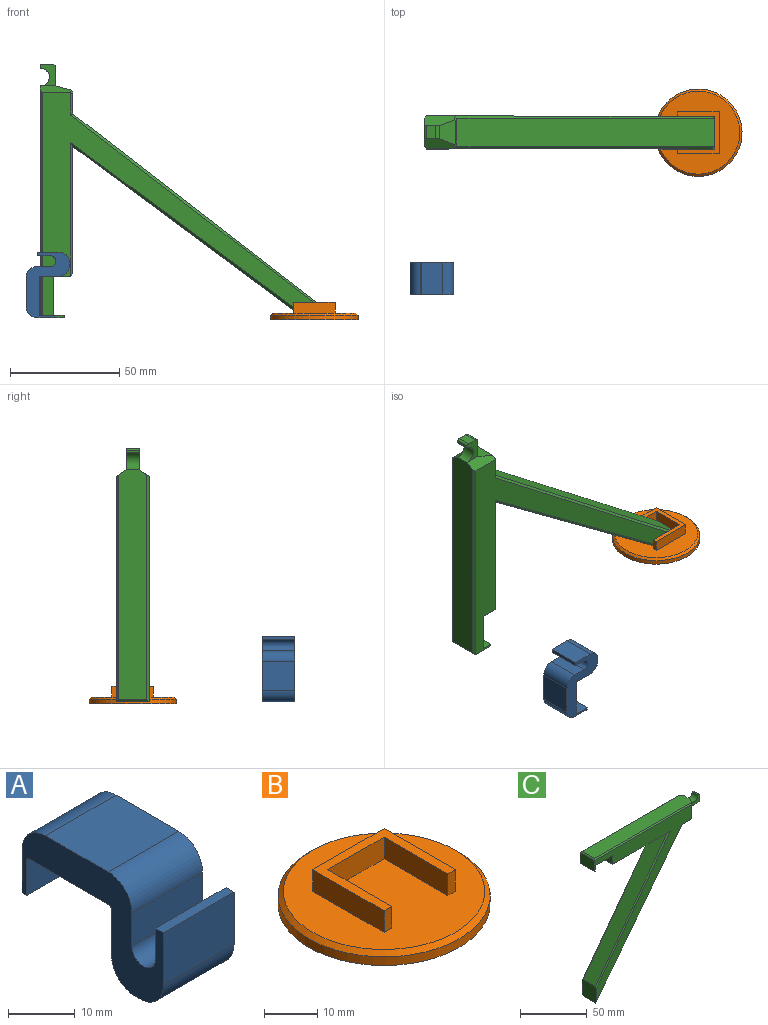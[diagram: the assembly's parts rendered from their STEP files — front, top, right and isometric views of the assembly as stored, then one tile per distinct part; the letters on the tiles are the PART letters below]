
ASSEMBLY  parts=3 mates=2
PART A: 20 faces, bbox 15x30x20 mm
  f0: plane 30x20mm, normal (1,0,0), area 245.4mm2, adj f2,f3,f4,f5,f6,f7,f8,f9
  f1: plane 30x20mm, normal (-1,0,0), area 245.4mm2, adj f2,f3,f4,f5,f6,f7,f8,f9
  f2: plane 15x1mm, normal (0,0,-1), area 15mm2, adj f0,f1,f15,f17
  f3: plane 15x8mm, normal (0,1,0), area 120mm2, adj f0,f1,f9,f16
  f4: plane 15x13.32mm, normal (0,0,1), area 199.8mm2, adj f0,f1,f14,f16
  f5: plane 15x9.64mm, normal (0,-1,0), area 144.7mm2, adj f0,f1,f13,f17
  f6: plane 15x5.74mm, normal (0,1,0), area 86mm2, adj f0,f1,f7,f13
  f7: cylinder r=2.5mm len=15mm, axis (1,0,0), area 117.8mm2, adj f0,f1,f6,f8
  f8: plane 15x6.09mm, normal (0,-1,0), area 91.4mm2, adj f0,f1,f7,f14
  f9: plane 15x1mm, normal (0,0,-1), area 15mm2, adj f0,f1,f3,f10
  f10: plane 15x6.5mm, normal (0,-1,0), area 97.5mm2, adj f0,f1,f9,f18
  f11: plane 17x15mm, normal (0,0,-1), area 255mm2, adj f0,f1,f18,f19
  f12: plane 15x8.5mm, normal (0,1,0), area 127.5mm2, adj f0,f1,f15,f19
  f13: plane 15x1.68mm, normal (0,0,1), area 25.2mm2, adj f0,f1,f5,f6
  f14: cylinder r=5mm len=15mm, axis (-1,0,0), area 117.8mm2, adj f0,f1,f4,f8
  f15: cylinder r=5mm len=15mm, axis (-1,0,0), area 117.8mm2, adj f0,f1,f2,f12
  f16: cylinder r=5mm len=15mm, axis (-1,0,0), area 117.8mm2, adj f0,f1,f3,f4
  f17: cylinder r=5mm len=15mm, axis (-1,0,0), area 117.8mm2, adj f0,f1,f2,f5
  f18: cylinder r=0.5mm len=15mm, axis (-1,0,0), area 11.8mm2, adj f0,f1,f10,f11
  f19: cylinder r=0.5mm len=15mm, axis (1,0,0), area 11.8mm2, adj f0,f1,f11,f12
PART B: 13 faces, bbox 40x40x8 mm
  f0: plane 5x2mm, normal (0,-1,0), area 10mm2, adj f1,f6,f10,f12
  f1: plane 19x19mm, normal (0,0,1), area 106mm2, adj f0,f5,f6,f7,f8,f9,f10,f11
  f2: cylinder r=20mm len=40mm, axis (0,0,1), area 251.3mm2, adj f3,f4
  f3: plane 40x40mm, normal (0,0,-1), area 1256.6mm2, adj f2
  f4: cone r=19mm half-angle=45deg, axis (0,0,-1), area 173.3mm2, adj f2,f12
  f5: plane 15x5mm, normal (0,-1,0), area 75mm2, adj f1,f6,f11,f12
  f6: plane 17x5mm, normal (-1,0,0), area 85mm2, adj f0,f1,f5,f12
  f7: plane 19x5mm, normal (0,1,0), area 95mm2, adj f1,f8,f10,f12
  f8: plane 19x5mm, normal (-1,0,0), area 95mm2, adj f1,f7,f9,f12
  f9: plane 5x2mm, normal (0,-1,0), area 10mm2, adj f1,f8,f11,f12
  f10: plane 19x5mm, normal (1,0,0), area 95mm2, adj f0,f1,f7,f12
  f11: plane 17x5mm, normal (1,0,0), area 85mm2, adj f1,f5,f9,f12
  f12: plane 38x38mm, normal (0,0,1), area 1028.1mm2, adj f0,f4,f5,f6,f7,f8,f9,f10
PART C: 39 faces, bbox 116x15x133 mm
  f0: plane 6x0.94mm, normal (0,0,1), area 5.6mm2, adj f6,f7,f26,f28
  f1: plane 105.07x13mm, normal (0,0,1), area 1357.6mm2, adj f7,f25,f27,f29,f35,f36
  f2: plane 11.33x7.25mm, normal (0.97,0,-0.25), area 65.5mm2, adj f3,f27,f29,f32,f33,f34
  f3: plane 9.05x6mm, normal (0,0,-1), area 54.3mm2, adj f2,f4,f26,f28
  f4: cylinder r=2mm len=6mm, axis (0,-1,0), area 11.7mm2, adj f3,f5,f26,f28
  f5: plane 6x4.35mm, normal (1,0,0), area 26.1mm2, adj f4,f6,f26,f28
  f6: cylinder r=1mm len=6mm, axis (0,-1,0), area 9.4mm2, adj f0,f5,f26,f28
  f7: cylinder r=4mm len=8mm, axis (0,-1,0), area 77.8mm2, adj f0,f1,f26,f27,f28,f29
  f8: plane 130.37x103.01mm, normal (0,-1,0), area 2384mm2, adj f11,f12,f13,f14,f16,f18,f22,f23
  f9: plane 13x10.02mm, normal (0,0,-1), area 129.4mm2, adj f19,f30,f31,f32,f33,f34
  f10: plane 130.37x103.01mm, normal (0,1,0), area 2384mm2, adj f11,f12,f13,f14,f16,f18,f20,f21
  f11: plane 15x5mm, normal (1,0,0), area 75mm2, adj f8,f10,f12,f14
  f12: plane 18x15mm, normal (0,0,-1), area 270mm2, adj f8,f10,f11,f16
  f13: plane 15x10mm, normal (-1,0,0), area 150mm2, adj f8,f10,f14,f25
  f14: plane 15x1mm, normal (0,0,-1), area 15mm2, adj f8,f10,f11,f13
  f15: plane 58.21x13mm, normal (0,0,-1), area 756.7mm2, adj f17,f24,f37,f38
  f16: plane 15x8mm, normal (-1,0,0), area 120mm2, adj f8,f10,f12,f24
  f17: plane 103x76.21mm, normal (-0.8,0,0.59), area 1665.6mm2, adj f15,f18,f21,f23
  f18: plane 15x15mm, normal (-1,0,0), area 221.7mm2, adj f8,f10,f17,f19,f20,f21,f22,f23
  f19: plane 118x91.21mm, normal (0.79,0,-0.61), area 1938.8mm2, adj f9,f18,f20,f22
  f20: plane 119x91.21mm, normal (0.56,0.71,-0.43), area 210.3mm2, adj f10,f18,f19,f30
  f21: plane 105.68x78.19mm, normal (-0.57,0.71,0.42), area 183.6mm2, adj f10,f17,f18,f37
  f22: plane 119x91.21mm, normal (0.56,-0.71,-0.43), area 210.3mm2, adj f8,f18,f19,f31
  f23: plane 105.68x78.19mm, normal (-0.57,-0.71,0.42), area 183.6mm2, adj f8,f17,f18,f38
  f24: plane 15x1mm, normal (-0.71,0,-0.71), area 19.8mm2, adj f15,f16,f37,f38
  f25: plane 15x1mm, normal (-0.71,0,0.71), area 19.8mm2, adj f1,f13,f35,f36
  f26: plane 9.93x7mm, normal (0,-1,0), area 42.1mm2, adj f0,f3,f4,f5,f6,f7,f27
  f27: plane 14.02x4.52mm, normal (0.83,-0.56,0), area 64.3mm2, adj f1,f2,f7,f8,f26,f33,f35
  f28: plane 9.93x7mm, normal (0,1,0), area 42.1mm2, adj f0,f3,f4,f5,f6,f7,f29
  f29: plane 14.02x4.52mm, normal (0.83,0.56,0), area 64.3mm2, adj f1,f2,f7,f10,f28,f32,f36
  f30: plane 10.3x1mm, normal (0,0.71,-0.71), area 13.8mm2, adj f9,f10,f20,f32
  f31: plane 10.3x1mm, normal (0,-0.71,-0.71), area 13.8mm2, adj f8,f9,f22,f33
  f32: plane 2.18x1.77mm, normal (0.58,0.4,-0.71), area 2.7mm2, adj f2,f9,f29,f30,f34
  f33: plane 2.18x1.77mm, normal (0.58,-0.4,-0.71), area 2.7mm2, adj f2,f9,f27,f31,f34
  f34: plane 10.82x0.97mm, normal (0.61,0,-0.79), area 13.1mm2, adj f2,f9,f32,f33
  f35: plane 103.69x1mm, normal (0,-0.71,0.71), area 145.5mm2, adj f1,f8,f25,f27
  f36: plane 103.69x1mm, normal (0,0.71,0.71), area 145.5mm2, adj f1,f10,f25,f29
  f37: plane 61.19x1mm, normal (0,0.71,-0.71), area 84.4mm2, adj f10,f15,f21,f24
  f38: plane 61.19x1mm, normal (0,-0.71,-0.71), area 84.4mm2, adj f8,f15,f23,f24
PLACE A rot(axis=(-0.58,-0.58,0.58),120deg) t=(-156.91,-143.42,-15.22)mm
PLACE B rot(axis=(0,0,-1),90deg) t=(-34.91,-69.12,-28.22)mm
PLACE C rot(axis=(0,-1,0),90deg) t=(-145.41,-61.62,-11.22)mm
MATE planar B.f2 <-> C.f18  axis (0,0,1) through (-34.91,-69.12,-28.22)mm
MATE parallel A.f3 <-> C.f13  axis (0,0,-1) through (-157.91,-135.92,-30.22)mm
